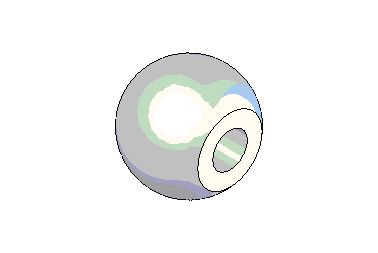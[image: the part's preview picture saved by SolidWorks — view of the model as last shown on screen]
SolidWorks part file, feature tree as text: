
SOLIDWORKS PART (.sldprt)
format: sldprt  version: not decoded by parser v0  size: 101,376 bytes
history: native  units: mm
features: sketch x3, material x1, revolve x1, cut_extrude x1, cut_revolve x1 (+13 scaffold rows collapsed)
feature tree (20):
  scaffold x13  (default folders/planes/origin — collapsed)
  material  "Material <not specified>"
  sketch  "Sketch1"  dims[D1=6.0mm]
  revolve  "Revolve1"  Angle=360deg
  sketch  "Sketch2"  dims[D1=9.44mm]
  cut_extrude  "Cut-Extrude2"  [1 undecoded]
  sketch  "Sketch3"  dims[c1.D1=4.0mm c1.D2=~1.700131mm c2.D2=45.0deg c2.D3=1.44mm]
  cut_revolve  "Cut-Revolve1"  Angle=360deg
decode coverage: 5 of 6 modeling features carry decoded parameters
note: ~ marks probable driven/reference dimensions
note: 1 parameter value undecoded
note: suppression state not decoded; provenance and decode notes live in map.json
